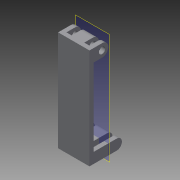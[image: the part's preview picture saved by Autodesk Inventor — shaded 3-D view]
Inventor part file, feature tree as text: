
AUTODESK INVENTOR PART (.ipt)
format: ipt  version: 2015 (Build 190159000, 159)  size: 220,672 bytes
history: native  units: mm
features: extrude x9, sketch x9, mirror x6, plane x3
ambient origin geometry x8: Origin, YZ Plane, XZ Plane, XY Plane, X Axis, Y Axis, Z Axis, Center Point
bodies: Solid1 (feature_tree)
feature tree (27):
  extrude  "Extrusion1"  Depth=15.0mm
  extrude  "Extrusion2"  Depth=5.0mm
  plane  "Work Plane1"
  mirror  "Mirror1"
  plane  "Work Plane2"
  mirror  "Mirror2"
  extrude  "Extrusion3"  Depth=10.0mm TaperAngle=0.0deg
  mirror  "Mirror3"
  extrude  "Extrusion4"  [1 undecoded]
  mirror  "Mirror4"
  mirror  "Mirror5"
  extrude  "Extrusion5"  Depth=45.0mm
  extrude  "Extrusion6"  Depth=3.0mm
  mirror  "Mirror6"
  extrude  "Extrusion7"  Depth=2.0mm TaperAngle=0.0deg
  extrude  "Extrusion8"  Depth=2.0mm TaperAngle=0.0deg
  plane  "Work Plane3"
  extrude  "Extrusion9"  Depth=1.0mm TaperAngle=0.0deg
  sketch  "Sketch1"  dims[d0=15.0mm d1=120.0mm]
  sketch  "Sketch3"  dims[d2=3.0mm d3=0.0mm d4=5.0mm]
  sketch  "Sketch6"  dims[d5=10.0mm d6=2.0mm d7=0.0mm]
  sketch  "Sketch9"  dims[d8=-7.5mm d10=-4.25mm]
  sketch  "Sketch10"  dims[d13=2.0mm d14=0.0mm d16=45.0mm]
  sketch  "Sketch11"  dims[d17=3.0mm d18=3.0mm]
  sketch  "Sketch12"  dims[d20=3.0mm d21=2.0mm d22=0.0mm]
  sketch  "Sketch13"  dims[d23=2.0mm d24=0.0mm d25=2.0mm d26=0.0mm]
  sketch  "Sketch15"  dims[d27=3.0mm d28=0.0mm d29=1.0mm d30=0.0mm d31=7.0mm d32=1.6mm d33=3.0mm d34=0.0mm]
note: 1 required parameter value undecoded (feature->parameter linkage not recoverable at this tier; creation-order binding heuristic only, values carry confidence <= 0.55)
